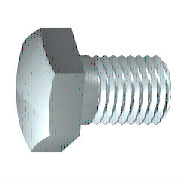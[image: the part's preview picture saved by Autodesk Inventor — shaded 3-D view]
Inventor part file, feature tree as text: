
AUTODESK INVENTOR PART (.ipt)
format: ipt  version: 2023.2 (Build 272271030, 271C)  size: 193,024 bytes
history: native  units: mm (DEFAULTED — no unit token found)
features: sketch x3, extrude x1, chamfer x1, plane x1
ambient origin geometry x7: Origin, YZ Plane, XZ Plane, X Axis, Y Axis, Z Axis, Center Point
bodies: Solid1 (feature_tree), Body (feature_tree)
feature tree (6):
  extrude  "Head"  Depth=9.6mm
  chamfer  "Chamfer1"  Distance=3.0mm
  plane  "Work Plane1"
  sketch  "Sketch1"  dims[d0=12.0mm d1=9.6mm]
  sketch  "Sketch2"  dims[d2=5.0mm]
  sketch  "Sketch4"  dims[d12=90.0deg d3=3.0mm d4=0.0mm d5=30.0deg d21=90.0deg d6=0.49076mm d7=0.49086mm d8=0.0mm d9=0.5001mm d10=6.88mm d11=8.0mm d13=0.49086mm d14=5.0mm d15=9.6mm d16=0.0mm d19=8.0mm d55=45.0deg d57=0.0mm d58=0.0mm]
